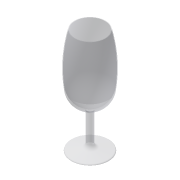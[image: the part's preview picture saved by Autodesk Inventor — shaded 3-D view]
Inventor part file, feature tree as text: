
AUTODESK INVENTOR PART (.ipt)
format: ipt  version: 2018 (Build 220112000, 112)  size: 230,400 bytes
history: native  units: mm
features: sketch x2, surface_op x2, revolve x2, other x2
ambient origin geometry x8: Origin, YZ Plane, XZ Plane, XY Plane, X Axis, Y Axis, Z Axis, Center Point
bodies: Solid1 (feature_tree)
feature tree (8):
  sketch  "Sketch3"  dims[d2=1.5mm d3=6.0mm d4=6.0mm d5=55.0mm d6=1.745329mm d8=27.5mm d10=100.0mm d11=46.0mm d12=200.0mm d13=90.0deg d14=0.8mm d15=199.2mm d20=4.0mm d28=5.0mm d29=0.0mm d30=90.0deg]
  surface_op  "Stitch Surface1"
  revolve  "Revolution1"  [1 undecoded]
  sketch  "Sketch2"  dims[d0=9.0mm d1=55.0mm]
  other  "Srf1"
  other  "Srf7"
  revolve  "RevolutionSrf1"  [1 undecoded]
  surface_op  "Boundary Patch4"
note: 2 required parameter values undecoded (feature->parameter linkage not recoverable at this tier; creation-order binding heuristic only, values carry confidence <= 0.55)
